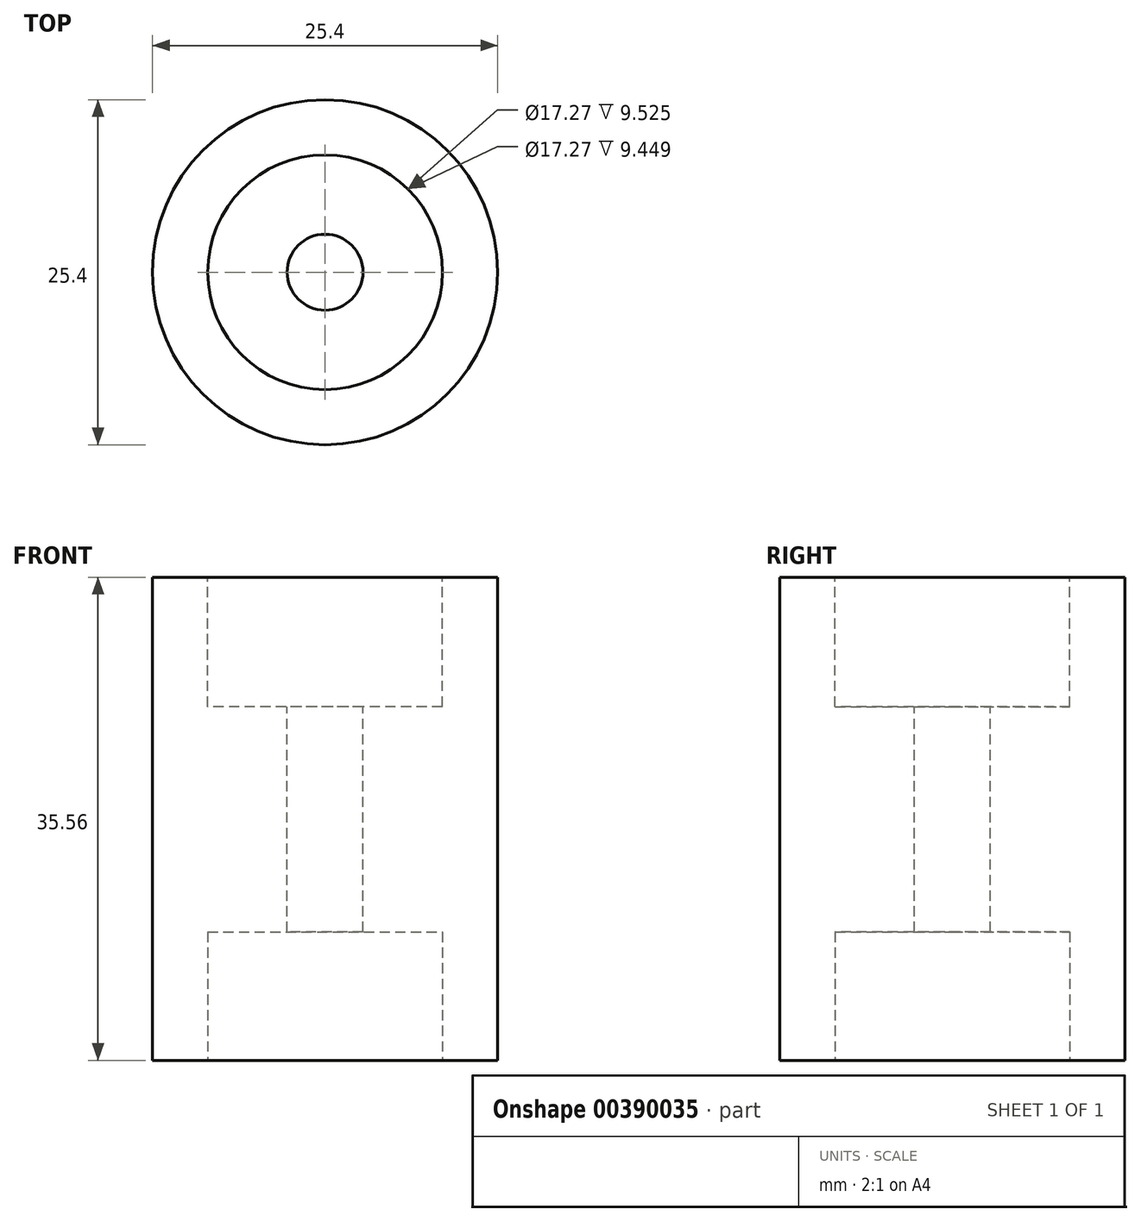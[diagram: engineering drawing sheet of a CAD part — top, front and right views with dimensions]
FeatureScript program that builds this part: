
annotation { "Feature Type Name" : "Feature", "Feature Type Description" : "" }
export const myFeature = defineFeature(function(context is Context, id is Id, definition is map)
    precondition{}
    {
        {
            var Q0;
            Q0=qCreatedBy(makeId("Top.planeOp"),FACE);
            var sketch = newSketch(context, id + "F0", { "sketchPlane" : qUnion([Q0])});
            skCircle(sketch, "E0", {"center": v(0, 0) * mm, "radius": 12.7 * mm});
            skSolve(sketch);
        }
        {
            var Q0;
            Q0=qSketchRegion(id+"F0",true);
            extrude(context, id + "F1", {"entities" : qUnion([Q0]), "depth" : 35.56 * mm});
        }
        {
            var Q0;
            Q0=makeQuery(id+"F1.opExtrude","CAP_FACE",FACE,{"disambiguationData":[OSD([sQuery(id+"F0.wireOp",EDGE,"E0")])],"isStart":false});
            var sketch = newSketch(context, id + "F2", { "sketchPlane" : qUnion([Q0])});
            skCircle(sketch, "E1", {"center": v(0, 0) * mm, "radius": 8.64 * mm});
            skSolve(sketch);
        }
        {
            var Q0;
            Q0=qSketchRegion(id+"F2",true);
            extrude(context, id + "F3", {"entities" : qUnion([Q0]), "operationType" : NewBodyOperationType.REMOVE, "oppositeDirection" : true, "depth" : 9.52 * mm});
        }
        {
            var Q0;
            Q0=makeQuery(id+"F3.boolean.opBoolean","COPY",FACE,{"derivedFrom":makeQuery(id+"F3.opExtrude","CAP_FACE",FACE,{"disambiguationData":[OSD([sQuery(id+"F2.wireOp",EDGE,"E1")])],"isStart":false})});
            var sketch = newSketch(context, id + "F4", { "sketchPlane" : qUnion([Q0])});
            skCircle(sketch, "E2", {"center": v(0, 0) * mm, "radius": 2.8 * mm});
            skSolve(sketch);
        }
        {
            var Q0;
            Q0=qSketchRegion(id+"F4",true);
            extrude(context, id + "F5", {"entities" : qUnion([Q0]), "operationType" : NewBodyOperationType.REMOVE, "oppositeDirection" : true, "depth" : 254 * mm});
        }
        {
            var Q0;
            Q0=makeQuery(id+"F1.opExtrude","CAP_FACE",FACE,{"disambiguationData":[OSD([sQuery(id+"F0.wireOp",EDGE,"E0")])],"isStart":true});
            var sketch = newSketch(context, id + "F6", { "sketchPlane" : qUnion([Q0])});
            skCircle(sketch, "E3", {"center": v(0, 0) * mm, "radius": 8.64 * mm});
            skSolve(sketch);
        }
        {
            var Q0;
            Q0=qCreatedBy(makeId("Right.planeOp"),FACE);
            cPlane(context, id + "F7", {"entities" : qUnion([Q0]), "cplaneType" : CPlaneType.OFFSET, "offset" : 7.62 * mm, "width" : 152.4 * mm, "height" : 152.4 * mm});
        }
        {
            var Q0;
            Q0=makeQuery(id+"F6.imprint","IMPRINT",FACE,{"disambiguationData":[TD([[makeQuery(id+"F6.imprint","IMPRINT",EDGE,{"derivedFrom":sQuery(id+"F6.wireOp",EDGE,"E3")}),1.0]])]});
            extrude(context, id + "F8", {"entities" : qUnion([Q0]), "operationType" : NewBodyOperationType.REMOVE, "oppositeDirection" : true, "depth" : 9.45 * mm});
        }
    });
